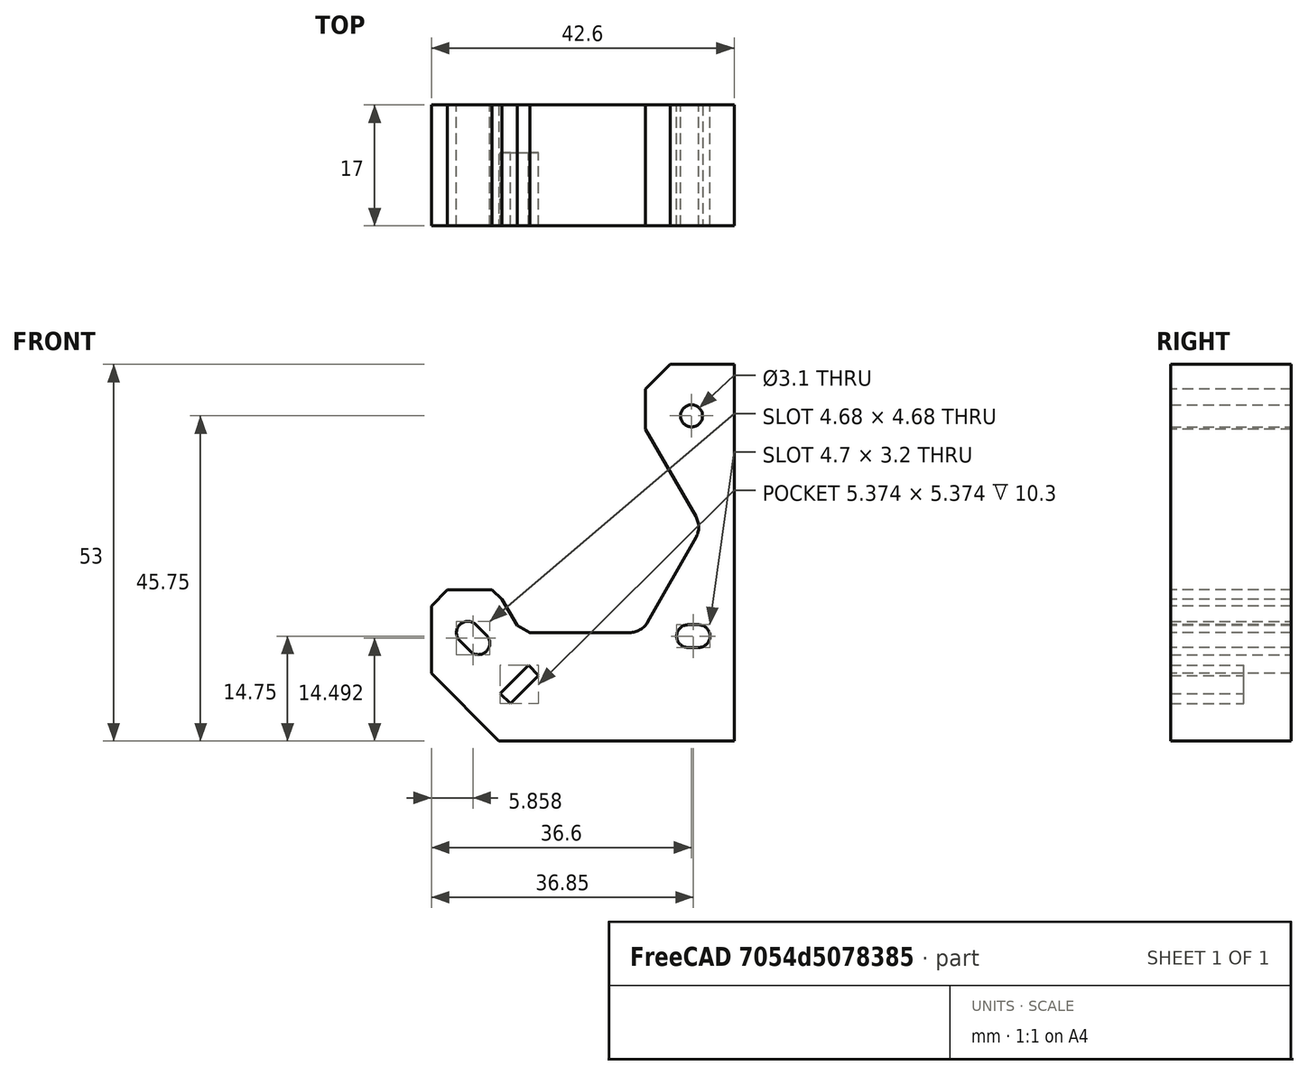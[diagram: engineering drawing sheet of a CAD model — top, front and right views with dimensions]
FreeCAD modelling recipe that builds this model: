
FCSTD DOCUMENT  (FreeCAD 0.19R)
Label: prusabeltmount
License: All rights reserved
LicenseURL: http://en.wikipedia.org/wiki/All_rights_reserved
objects: Mesh::Feature×1, Sketcher::SketchObject×1, PartDesign::Body×1, Part::Box×1, Part::Extrusion×1, Part::Cut×1
note: 5 computed .brp shape members not serialized (recipe doc carries the construction recipe); baked Part::Feature solids carry a one-line shape summary decoded from their .brp

FEATURE [Mesh::Feature] x_end_motor  label="x-end-motor"
  Placement = pos=(5.3e-15,23.5,0) rot=(0,0,1;1.5708rad)
FEATURE [Sketcher::SketchObject] Sketch
  MapMode = 5
  Placement = pos=(0,0,0) rot=(1,0,0;1.5708rad)
  Support = -> [XZ_Plane]
  sketch-geometry (26):
    g0: Circle CenterX=-16.5 CenterY=45.75 CenterZ=0 NormalX=0 NormalY=0 NormalZ=1 AngleXU=0 Radius=1.55
    g1: ArcOfCircle CenterX=-17 CenterY=14.75 CenterZ=0 NormalX=0 NormalY=0 NormalZ=1 AngleXU=0 Radius=1.6 StartAngle=1.5708 EndAngle=4.71239
    g2: ArcOfCircle CenterX=-15.5 CenterY=14.75 CenterZ=0 NormalX=0 NormalY=0 NormalZ=1 AngleXU=0 Radius=1.6 StartAngle=4.71239 EndAngle=7.85398
    g3: LineSegment StartX=-17 StartY=13.15 StartZ=0 EndX=-15.5 EndY=13.15 EndZ=0
    g4: LineSegment StartX=-17 StartY=16.35 StartZ=0 EndX=-15.5 EndY=16.35 EndZ=0
    g5: ArcOfCircle CenterX=-47.9849 CenterY=15.2349 CenterZ=0 NormalX=0 NormalY=0 NormalZ=1 AngleXU=0 Radius=1.6 StartAngle=0.785398 EndAngle=3.92699
    g6: ArcOfCircle CenterX=-46.5 CenterY=13.75 CenterZ=0 NormalX=0 NormalY=0 NormalZ=1 AngleXU=0 Radius=1.6 StartAngle=3.92699 EndAngle=7.06858
    g7: LineSegment StartX=-49.1163 StartY=14.1036 StartZ=0 EndX=-47.6314 EndY=12.6186 EndZ=0
    g8: LineSegment StartX=-46.8536 StartY=16.3663 StartZ=0 EndX=-45.3686 EndY=14.8814 EndZ=0
    g9: LineSegment StartX=-10.5 StartY=53 StartZ=0 EndX=-10.5 EndY=0 EndZ=0
    g10: LineSegment StartX=-10.5 StartY=53 StartZ=0 EndX=-19.5 EndY=53 EndZ=0
    g11: LineSegment StartX=-19.5 StartY=53 StartZ=0 EndX=-23 EndY=49.5 EndZ=0
    g12: LineSegment StartX=-23 StartY=49.5 StartZ=0 EndX=-23 EndY=43.85 EndZ=0
    g13: ArcOfCircle CenterX=-18.5 CenterY=30.1 CenterZ=0 NormalX=0 NormalY=0 NormalZ=1 AngleXU=0 Radius=3 StartAngle=5.7654 EndAngle=6.80835
    g14: LineSegment StartX=-23 StartY=43.85 StartZ=0 EndX=-15.9043 EndY=31.6041 EndZ=0
    g15: ArcOfCircle CenterX=-25.25 CenterY=18.25 CenterZ=0 NormalX=0 NormalY=0 NormalZ=1 AngleXU=0 Radius=3 StartAngle=4.71239 EndAngle=5.7654
    g16: LineSegment StartX=-15.8932 StartY=28.6151 StartZ=0 EndX=-22.6432 EndY=16.7651 EndZ=0
    g17: LineSegment StartX=-25.25 StartY=15.25 StartZ=0 EndX=-39.25 EndY=15.25 EndZ=0
    g18: LineSegment StartX=-39.25 StartY=15.25 StartZ=0 EndX=-41.05 EndY=16.25 EndZ=0
    g19: LineSegment StartX=-41.05 StartY=16.25 StartZ=0 EndX=-43.2 EndY=19.95 EndZ=0
    g20: LineSegment StartX=-43.2 StartY=19.95 StartZ=0 EndX=-44.6 EndY=21.25 EndZ=0
    g21: LineSegment StartX=-44.6 StartY=21.25 StartZ=0 EndX=-50.85 EndY=21.25 EndZ=0
    g22: LineSegment StartX=-50.85 StartY=21.25 StartZ=0 EndX=-53.1 EndY=19 EndZ=0
    g23: LineSegment StartX=-53.1 StartY=19 StartZ=0 EndX=-53.1 EndY=9.5 EndZ=0
    g24: LineSegment StartX=-53.1 StartY=9.5 StartZ=0 EndX=-43.6 EndY=0 EndZ=0
    g25: LineSegment StartX=-43.6 StartY=0 StartZ=0 EndX=-10.5 EndY=0 EndZ=0
  constraints (72):
    c: Radius(g0) = 1.55
    c: DistanceX(g0) = -16.5
    c: DistanceY(g0) = 45.75
    c: Tangent(g1,g4) = 1.5708
    c: Tangent(g1,g3) = -1.5708
    c: Tangent(g3,g2) = -1.5708
    c: Tangent(g4,g2) = 1.5708
    c: Horizontal(g3)
    c: Equal(g1,g2)
    c: DistanceY(g2,g2) = 3.2
    c: DistanceX(g2) = -15.5
    c: DistanceY(g2) = 14.75
    c: DistanceX(g1,g2) = 1.5
    c: Tangent(g5,g8) = 1.5708
    c: Tangent(g5,g7) = -1.5708
    c: Tangent(g7,g6) = -1.5708
    c: Tangent(g8,g6) = 1.5708
    c: Equal(g5,g6)
    c: Distance(g6,g6) = 3.2
    c: Distance(g5,g6) = 2.1
    c: Angle(g8) = -0.785398
    c: DistanceX(g6,g2) = 31
    c: DistanceY(g6,g2) = 1
    c: Vertical(g9)
    c: DistanceX(g0,g9) = 6
    c: DistanceY(g0,g9) = 7.25
    c: Coincident(g9,g10)
    c: Horizontal(g10)
    c: Coincident(g10,g11)
    c: Coincident(g11,g12)
    c: Vertical(g12)
    c: DistanceY(g9,g9) = 53
    c: Radius(g13) = 3
    c: Coincident(g14,g12)
    c: Tangent(g13,g14) = 1.5708
    c: DistanceX(g10,g10) = 9
    c: DistanceX(g11,g10) = 3.5
    c: DistanceY(g11,g10) = 3.5
    c: Horizontal(g17)
    c: Tangent(g13,g16) = 1.5708
    c: DistanceX(g13,g9) = 8
    c: DistanceY(g13,g12) = 13.75
    c: Tangent(g16,g15) = 1.5708
    c: Equal(g15,g13)
    c: DistanceY(g12,g11) = 5.65
    c: DistanceY(g15,g13) = 11.85
    c: DistanceX(g15,g9) = 14.75
    c: Tangent(g15,g17) = 1.5708
    c: Coincident(g17,g18)
    c: Coincident(g18,g19)
    c: Coincident(g19,g20)
    c: Coincident(g20,g21)
    c: Horizontal(g21)
    c: Coincident(g21,g22)
    c: Coincident(g22,g23)
    c: Vertical(g23)
    c: Coincident(g23,g24)
    c: Coincident(g24,g25)
    c: Coincident(g25,g9)
    c: Horizontal(g25)
    c: DistanceX(g24,g9) = 33.1
    c: DistanceX(g23,g24) = 9.5
    c: DistanceY(g24,g23) = 9.5
    c: DistanceY(g23,g22) = 9.5
    c: DistanceX(g22,g21) = 2.25
    c: DistanceY(g22,g21) = 2.25
    c: DistanceX(g21,g21) = 6.25
    c: DistanceX(g17,g15) = 14
    c: DistanceX(g18,g17) = 1.8
    c: DistanceX(g19,g18) = 2.15
    c: DistanceY(g17,g18) = 1
    c: DistanceY(g18,g19) = 3.7
FEATURE [PartDesign::Body] Body
  Group = -> [Sketch]
  Origin = -> Origin
FEATURE [Part::Box] Box  label="Cube"
  AttacherType = Attacher::AttachEngine3D
  Height = 2
  Length = 5.6
  Placement = pos=(-42,0,5.26299) rot=(0,-1,0;0.785398rad)
  Width = 10.3
FEATURE [Part::Extrusion] Extrude
  Base = -> Sketch
  Dir = (0,-1,-2e-16)
  DirMode = 2
  FaceMakerClass = Part::FaceMakerBullseye
  LengthFwd = 0
  LengthRev = 17
  Solid = true
  Symmetric = false
FEATURE [Part::Cut] Cut
  Base = -> Extrude
  Tool = -> Box
